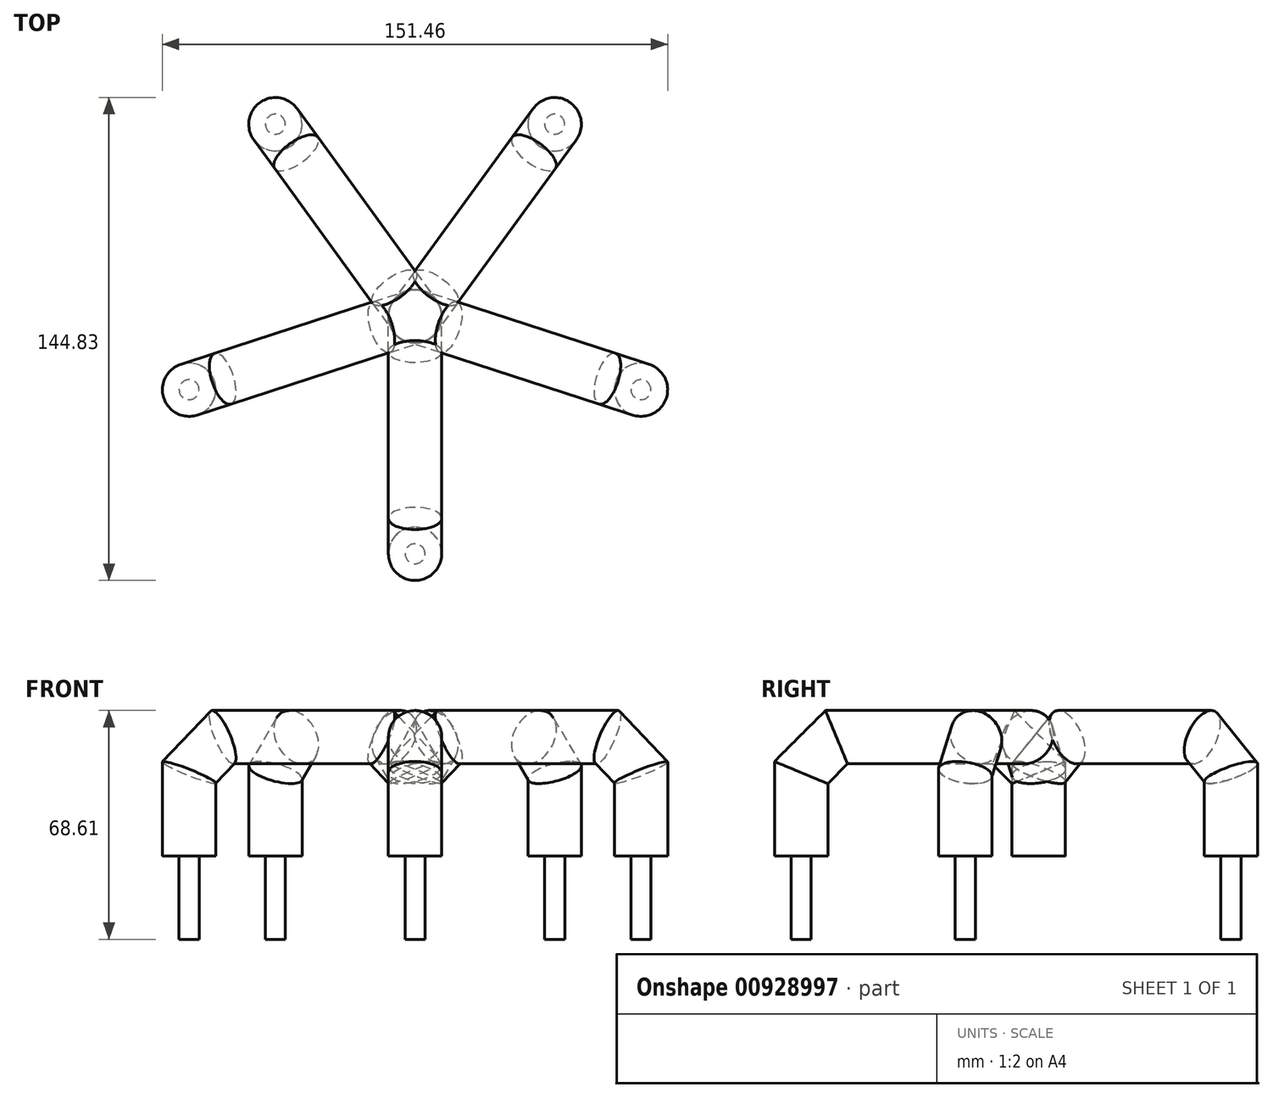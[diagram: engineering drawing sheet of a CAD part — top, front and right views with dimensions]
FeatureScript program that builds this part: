
annotation { "Feature Type Name" : "Feature", "Feature Type Description" : "" }
export const myFeature = defineFeature(function(context is Context, id is Id, definition is map)
    precondition{}
    {
        {
            var Q0;
            Q0=qCreatedBy(makeId("Front.planeOp"),FACE);
            var sketch = newSketch(context, id + "F0", { "sketchPlane" : qUnion([Q0])});
            skCircle(sketch, "E0", {"center": v(70, 70) * mm, "radius": 8 * mm});
            skSolve(sketch);
        }
        {
            var Q0;
            Q0=qCreatedBy(makeId("Right.planeOp"),FACE);
            var sketch = newSketch(context, id + "F1", { "sketchPlane" : qUnion([Q0])});
            skLineSegment(sketch, "E1", {"start": v(0, 70) * mm, "end": v(25, 70) * mm});
            skLineSegment(sketch, "E2", {"start": v(25, 70) * mm, "end": v(35.6, 59.4) * mm});
            skLineSegment(sketch, "E3", {"start": v(35.6, 59.4) * mm, "end": v(35.6, 34.4) * mm});
            skPoint(sketch, "E4.visualSharp", {"position": v(25, 70) * mm});
            skLineSegment(sketch, "E4.filletArc", {"start": v(25, 70) * mm, "end": v(25, 70) * mm});
            skSolve(sketch);
        }
        {
            var Q0;
            Q0 = qSketchRegion(id + "F0", true);
            var Q1;
            Q1 = qConstructionFilter(qBodyType(qCreatedBy(id + "F1" ,EDGE), BodyType.WIRE), ConstructionObject.NO);
            sweep(context, id + "F2", {"profiles" : qUnion([Q0]), "path" : qUnion([Q1])});
        }
        {
            var Q0;
            Q0=makeQuery(id+"F2.opSweep","SWEPT_BODY",BODY,{"disambiguationData":[OSD([sQuery(id+"F0.wireOp",EDGE,"E0"),sQuery(id+"F1.wireOp",EDGE,"E3")])]});
            var Q1;
            Q1=qCreatedBy(makeId("Front.planeOp"),FACE);
            mirror(context, id + "F3", {"operationType" : NewBodyOperationType.ADD, "entities" : qUnion([Q0]), "mirrorPlane" : qUnion([Q1])});
        }
        {
            var Q0;
            Q0=makeQuery(id+"F3.opPattern","COPY",FACE,{"derivedFrom":makeQuery(id+"F2.opSweep","CAP_FACE",FACE,{"disambiguationData":[OSD([sQuery(id+"F0.wireOp",EDGE,"E0"),sQuery(id+"F1.wireOp",VERTEX,"E3.end")])],"isStart":false}),"instanceName":"1"});
            var sketch = newSketch(context, id + "F4", { "sketchPlane" : qUnion([Q0])});
            skCircle(sketch, "E5.0", {"center": v(70, 35.6) * mm, "radius": 8 * mm});
            skCircle(sketch, "E6.0", {"center": v(70, 35.6) * mm, "radius": 3 * mm});
            skSolve(sketch);
        }
        {
            var Q0;
            Q0=makeQuery(id+"F4.imprint","IMPRINT",FACE,{"disambiguationData":[TD([[makeQuery(id+"F4.imprint","IMPRINT",EDGE,{"derivedFrom":sQuery(id+"F4.wireOp",EDGE,"E6.0")}),1.0]])]});
            extrude(context, id + "F5", {"entities" : qUnion([Q0]), "operationType" : NewBodyOperationType.ADD, "depth" : 25 * mm, "offsetDistance" : 25 * mm});
        }
        {
            var Q0;
            Q0=makeQuery(id+"F2.opSweep","SWEPT_BODY",BODY,{"disambiguationData":[OSD([sQuery(id+"F0.wireOp",EDGE,"E0"),sQuery(id+"F1.wireOp",EDGE,"E3")])]});
            var Q1;
            Q1=makeQuery(id+"F2.opSweep","SWEPT_FACE",FACE,{"disambiguationData":[OSD([sQuery(id+"F0.wireOp",EDGE,"E0"),sQuery(id+"F1.wireOp",EDGE,"E3")])]});
            circularPattern(context, id + "F6", {"entities" : qUnion([Q0]), "axis" : qUnion([Q1]), "angle" : 360 * degree, "instanceCount" : 5, "equalSpace" : true});
        }
    });
